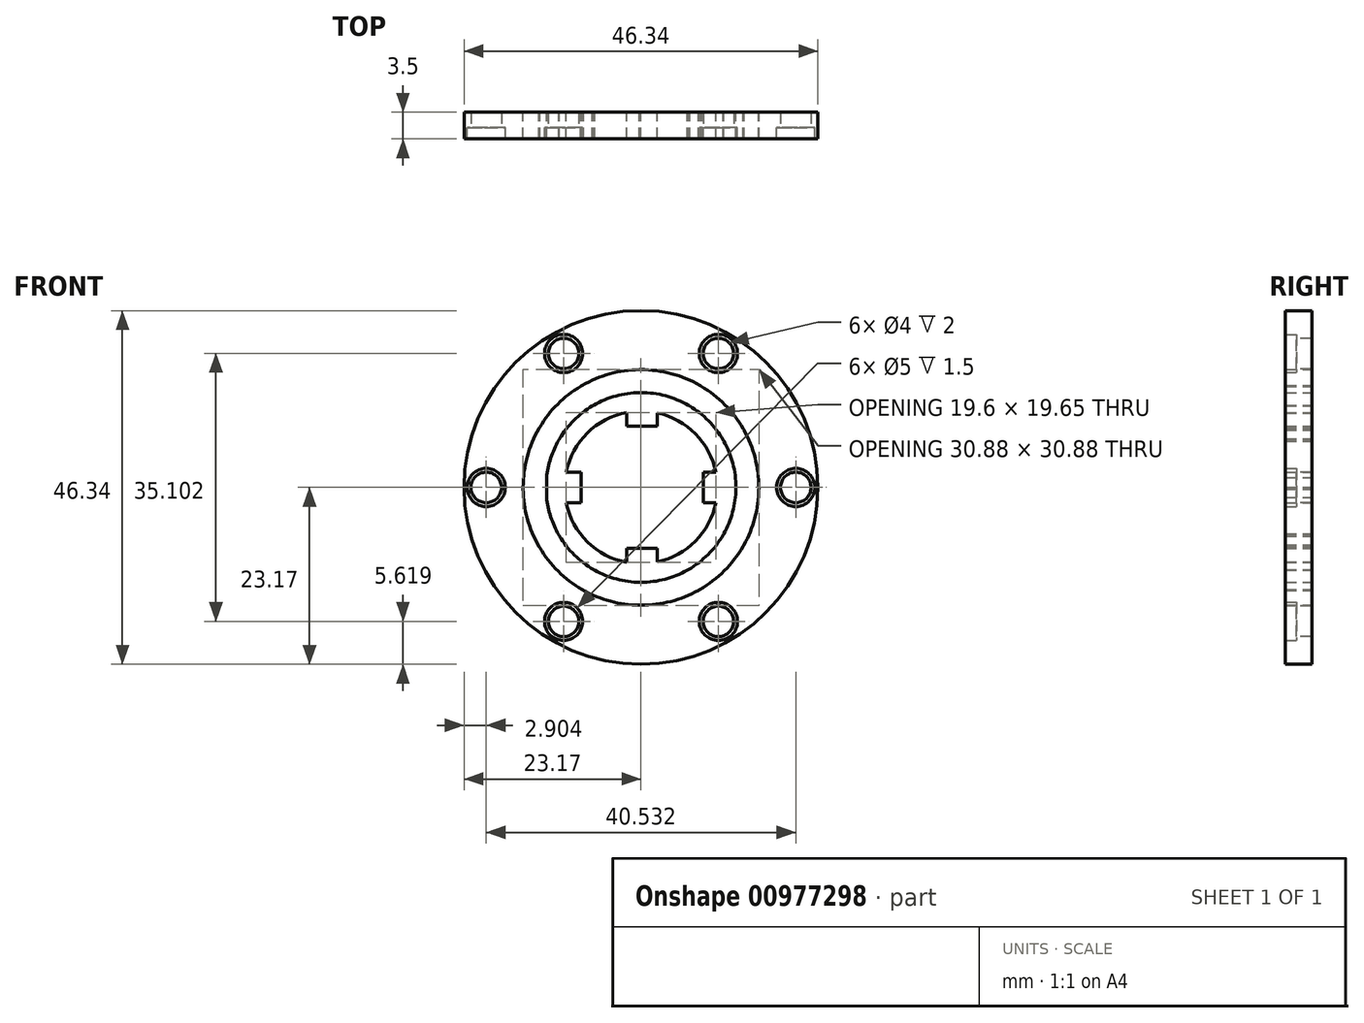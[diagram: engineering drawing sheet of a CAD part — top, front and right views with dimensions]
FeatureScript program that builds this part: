
annotation { "Feature Type Name" : "Feature", "Feature Type Description" : "" }
export const myFeature = defineFeature(function(context is Context, id is Id, definition is map)
    precondition{}
    {
        {
            var Q0;
            Q0=qCreatedBy(makeId("Front.planeOp"),FACE);
            var sketch = newSketch(context, id + "F0", { "sketchPlane" : qUnion([Q0])});
            skCircle(sketch, "E0", {"center": v(0, 0) * mm, "radius": 10 * mm});
            skPoint(sketch, "E1.left.end.orphan", {"position": v(-12.36, 2) * mm});
            skPoint(sketch, "E2.orphan", {"position": v(-12.64, -2) * mm});
            skPoint(sketch, "E1.right.end.orphan", {"position": v(12.64, 2) * mm});
            skPoint(sketch, "E3.trimOffspring.end.orphan", {"position": v(12.36, -2) * mm});
            skPoint(sketch, "E4.top.end.orphan", {"position": v(1.86, -12.5) * mm});
            skPoint(sketch, "E4.top.start.orphan", {"position": v(-1.86, -12.5) * mm});
            skPoint(sketch, "E4.bottom.end.orphan", {"position": v(1.86, 12.5) * mm});
            skPoint(sketch, "E4.bottom.start.orphan", {"position": v(-1.86, 12.5) * mm});
            skLineSegment(sketch, "E5.bottom", {"start": v(12.64, 2) * mm, "end": v(8.14, 2) * mm});
            skLineSegment(sketch, "E5.top", {"start": v(12.64, -2) * mm, "end": v(8.14, -2) * mm});
            skLineSegment(sketch, "E5.left", {"start": v(12.64, 2) * mm, "end": v(12.64, -2) * mm});
            skLineSegment(sketch, "E5.right", {"start": v(8.14, 2) * mm, "end": v(8.14, -2) * mm});
            skLineSegment(sketch, "E6.bottom", {"start": v(-1.86, 12.5) * mm, "end": v(2.14, 12.5) * mm});
            skLineSegment(sketch, "E6.top", {"start": v(-1.86, 8) * mm, "end": v(2.14, 8) * mm});
            skLineSegment(sketch, "E6.left", {"start": v(-1.86, 12.5) * mm, "end": v(-1.86, 8) * mm});
            skLineSegment(sketch, "E6.right", {"start": v(2.14, 12.5) * mm, "end": v(2.14, 8) * mm});
            skLineSegment(sketch, "E7.bottom", {"start": v(-12.36, 2) * mm, "end": v(-7.86, 2) * mm});
            skLineSegment(sketch, "E7.top", {"start": v(-12.36, -2) * mm, "end": v(-7.86, -2) * mm});
            skLineSegment(sketch, "E7.left", {"start": v(-12.36, 2) * mm, "end": v(-12.36, -2) * mm});
            skLineSegment(sketch, "E7.right", {"start": v(-7.86, 2) * mm, "end": v(-7.86, -2) * mm});
            skLineSegment(sketch, "E8.bottom", {"start": v(-1.86, -12.5) * mm, "end": v(2.14, -12.5) * mm});
            skLineSegment(sketch, "E8.top", {"start": v(-1.86, -8) * mm, "end": v(2.14, -8) * mm});
            skLineSegment(sketch, "E8.left", {"start": v(-1.86, -12.5) * mm, "end": v(-1.86, -8) * mm});
            skLineSegment(sketch, "E8.right", {"start": v(2.14, -12.5) * mm, "end": v(2.14, -8) * mm});
            skCircle(sketch, "E9", {"center": v(0, 0) * mm, "radius": 12.43 * mm});
            skCircle(sketch, "E10", {"center": v(0, 0) * mm, "radius": 15.43 * mm});
            skArc(sketch, "E11", {"start": v(0, 15.43) * mm, "mid": v(-1.6, 13.93) * mm, "end": v(0, 12.43) * mm});
            skArc(sketch, "E12", {"start": v(0, 15.27) * mm, "mid": v(-1.44, 13.93) * mm, "end": v(0, 12.6) * mm});
            skLineSegment(sketch, "E13", {"start": v(0, 15.43) * mm, "end": v(0, 15.27) * mm});
            skLineSegment(sketch, "E14", {"start": v(0, 12.6) * mm, "end": v(0, 12.43) * mm});
            skLineSegment(sketch, "E15", {"start": v(0, 15.69) * mm, "end": v(0, 12.13) * mm, "construction": true});
            skArc(sketch, "E16.MirrorCS", {"start": v(0, -15.43) * mm, "mid": v(-1.6, -13.93) * mm, "end": v(0, -12.43) * mm});
            skArc(sketch, "E17.MirrorCS", {"start": v(0, -15.27) * mm, "mid": v(-1.44, -13.93) * mm, "end": v(0, -12.6) * mm});
            skLineSegment(sketch, "E18.MirrorCS", {"start": v(0, -15.69) * mm, "end": v(0, -12.13) * mm, "construction": true});
            skArc(sketch, "E19.MirrorCS", {"start": v(15.43, 0) * mm, "mid": v(13.93, -1.6) * mm, "end": v(12.43, 0) * mm});
            skArc(sketch, "E20.MirrorCS", {"start": v(15.27, 0) * mm, "mid": v(13.93, -1.44) * mm, "end": v(12.6, 0) * mm});
            skLineSegment(sketch, "E21.MirrorCS", {"start": v(15.69, 0) * mm, "end": v(12.13, 0) * mm, "construction": true});
            skArc(sketch, "E22.MirrorCS", {"start": v(-15.27, 0) * mm, "mid": v(-13.93, -1.44) * mm, "end": v(-12.6, 0) * mm});
            skArc(sketch, "E23.MirrorCS", {"start": v(-15.43, 0) * mm, "mid": v(-13.93, -1.6) * mm, "end": v(-12.43, 0) * mm});
            skLineSegment(sketch, "E24.MirrorCS", {"start": v(-15.69, 0) * mm, "end": v(-12.13, 0) * mm, "construction": true});
            skArc(sketch, "E25.MirrorCS", {"start": v(13.37, 7.72) * mm, "mid": v(12.87, 5.58) * mm, "end": v(10.76, 6.21) * mm});
            skArc(sketch, "E26.MirrorCS", {"start": v(13.22, 7.63) * mm, "mid": v(12.78, 5.72) * mm, "end": v(10.9, 6.3) * mm});
            skLineSegment(sketch, "E27.MirrorCS", {"start": v(13.59, 7.84) * mm, "end": v(10.5, 6.07) * mm, "construction": true});
            skLineSegment(sketch, "E28.MirrorCS", {"start": v(-7.84, 13.59) * mm, "end": v(-6.07, 10.5) * mm, "construction": true});
            skArc(sketch, "E29.MirrorCS", {"start": v(-7.63, 13.22) * mm, "mid": v(-8.21, 11.35) * mm, "end": v(-6.3, 10.9) * mm});
            skArc(sketch, "E30.MirrorCS", {"start": v(-7.72, 13.37) * mm, "mid": v(-8.35, 11.26) * mm, "end": v(-6.21, 10.76) * mm});
            skLineSegment(sketch, "E31.MirrorCS", {"start": v(-13.59, -7.84) * mm, "end": v(-10.5, -6.07) * mm, "construction": true});
            skArc(sketch, "E32.MirrorCS", {"start": v(-13.22, -7.63) * mm, "mid": v(-11.35, -8.21) * mm, "end": v(-10.9, -6.3) * mm});
            skArc(sketch, "E33.MirrorCS", {"start": v(-13.37, -7.72) * mm, "mid": v(-11.26, -8.35) * mm, "end": v(-10.76, -6.21) * mm});
            skLineSegment(sketch, "E34.MirrorCS", {"start": v(7.84, -13.59) * mm, "end": v(6.07, -10.5) * mm, "construction": true});
            skArc(sketch, "E35.MirrorCS", {"start": v(7.63, -13.22) * mm, "mid": v(5.72, -12.78) * mm, "end": v(6.3, -10.9) * mm});
            skArc(sketch, "E36.MirrorCS", {"start": v(7.72, -13.37) * mm, "mid": v(5.58, -12.87) * mm, "end": v(6.21, -10.76) * mm});
            skArc(sketch, "E37.MirrorCS", {"start": v(-13.37, 7.72) * mm, "mid": v(-11.26, 8.35) * mm, "end": v(-10.76, 6.21) * mm});
            skArc(sketch, "E38.MirrorCS", {"start": v(-13.22, 7.63) * mm, "mid": v(-11.35, 8.21) * mm, "end": v(-10.9, 6.3) * mm});
            skLineSegment(sketch, "E39.MirrorCS", {"start": v(-13.59, 7.84) * mm, "end": v(-10.5, 6.07) * mm, "construction": true});
            skArc(sketch, "E40.MirrorCS", {"start": v(7.63, 13.22) * mm, "mid": v(8.21, 11.35) * mm, "end": v(6.3, 10.9) * mm});
            skLineSegment(sketch, "E41.MirrorCS", {"start": v(7.84, 13.59) * mm, "end": v(6.07, 10.5) * mm, "construction": true});
            skArc(sketch, "E42.MirrorCS", {"start": v(7.72, 13.37) * mm, "mid": v(8.35, 11.26) * mm, "end": v(6.21, 10.76) * mm});
            skArc(sketch, "E43.MirrorCS", {"start": v(13.37, -7.72) * mm, "mid": v(12.87, -5.58) * mm, "end": v(10.76, -6.21) * mm});
            skArc(sketch, "E44.MirrorCS", {"start": v(13.22, -7.63) * mm, "mid": v(12.78, -5.72) * mm, "end": v(10.9, -6.3) * mm});
            skLineSegment(sketch, "E45.MirrorCS", {"start": v(13.59, -7.84) * mm, "end": v(10.5, -6.07) * mm, "construction": true});
            skArc(sketch, "E46.MirrorCS", {"start": v(-7.72, -13.37) * mm, "mid": v(-5.58, -12.87) * mm, "end": v(-6.21, -10.76) * mm});
            skArc(sketch, "E47.MirrorCS", {"start": v(-7.63, -13.22) * mm, "mid": v(-5.72, -12.78) * mm, "end": v(-6.3, -10.9) * mm});
            skLineSegment(sketch, "E48.MirrorCS", {"start": v(-7.84, -13.59) * mm, "end": v(-6.07, -10.5) * mm, "construction": true});
            skCircle(sketch, "E49", {"center": v(0, 0) * mm, "radius": 20.27 * mm, "construction": true});
            skCircle(sketch, "E50", {"center": v(0, 0) * mm, "radius": 23.17 * mm});
            skLineSegment(sketch, "E51.0", {"start": v(20.27, 0) * mm, "end": v(10.13, -17.55) * mm});
            skLineSegment(sketch, "E51.1", {"start": v(10.13, -17.55) * mm, "end": v(-10.13, -17.55) * mm});
            skLineSegment(sketch, "E51.2", {"start": v(-10.13, -17.55) * mm, "end": v(-20.27, 0) * mm});
            skLineSegment(sketch, "E51.3", {"start": v(-20.27, 0) * mm, "end": v(-10.13, 17.55) * mm});
            skLineSegment(sketch, "E51.4", {"start": v(-10.13, 17.55) * mm, "end": v(10.13, 17.55) * mm});
            skLineSegment(sketch, "E51.5", {"start": v(10.13, 17.55) * mm, "end": v(20.27, 0) * mm});
            skSolve(sketch);
        }
        {
            var Q0;
            {var subQ3=sQuery(id+"F0.wireOp",EDGE,"E6.left");var subQ5=sQuery(id+"F0.wireOp",EDGE,"E0");var subQ6=makeQuery(id+"F0.imprint","INTERSECT",VERTEX,{"derivedFrom":[subQ5,subQ3]});Q0=makeQuery(id+"F0.imprint","IMPRINT",FACE,{"disambiguationData":[TD([[makeQuery(id+"F0.imprint","IMPRINT",EDGE,{"disambiguationData":[TD([[subQ6,-1.0]])],"derivedFrom":subQ5}),-1.0]])]});}
            var Q1;
            {var subQ5=sQuery(id+"F0.wireOp",EDGE,"E0");var subQ8=sQuery(id+"F0.wireOp",EDGE,"E7.bottom");var subQ9=makeQuery(id+"F0.imprint","INTERSECT",VERTEX,{"derivedFrom":[subQ5,subQ8]});Q1=makeQuery(id+"F0.imprint","IMPRINT",FACE,{"disambiguationData":[TD([[makeQuery(id+"F0.imprint","IMPRINT",EDGE,{"disambiguationData":[TD([[subQ9,-1.0]])],"derivedFrom":subQ5}),-1.0]])]});}
            var Q2;
            {var subQ5=sQuery(id+"F0.wireOp",EDGE,"E7.right");Q2=makeQuery(id+"F0.imprint","IMPRINT",FACE,{"disambiguationData":[TD([[makeQuery(id+"F0.imprint","IMPRINT",EDGE,{"derivedFrom":subQ5}),-1.0]])]});}
            var Q3;
            {var subQ3=sQuery(id+"F0.wireOp",EDGE,"E7.top");var subQ6=sQuery(id+"F0.wireOp",EDGE,"E0");var subQ9=makeQuery(id+"F0.imprint","INTERSECT",VERTEX,{"derivedFrom":[subQ6,subQ3]});Q3=makeQuery(id+"F0.imprint","IMPRINT",FACE,{"disambiguationData":[TD([[makeQuery(id+"F0.imprint","IMPRINT",EDGE,{"disambiguationData":[TD([[subQ9,-1.0]])],"derivedFrom":subQ6}),-1.0]])]});}
            var Q4;
            {var subQ1=sQuery(id+"F0.wireOp",EDGE,"E8.left");var subQ5=sQuery(id+"F0.wireOp",EDGE,"E0");var subQ6=makeQuery(id+"F0.imprint","INTERSECT",VERTEX,{"derivedFrom":[subQ5,subQ1]});Q4=makeQuery(id+"F0.imprint","IMPRINT",FACE,{"disambiguationData":[TD([[makeQuery(id+"F0.imprint","IMPRINT",EDGE,{"disambiguationData":[TD([[subQ6,-1.0]])],"derivedFrom":subQ5}),-1.0]])]});}
            var Q5;
            {var subQ5=sQuery(id+"F0.wireOp",EDGE,"E8.top");Q5=makeQuery(id+"F0.imprint","IMPRINT",FACE,{"disambiguationData":[TD([[makeQuery(id+"F0.imprint","IMPRINT",EDGE,{"derivedFrom":subQ5}),-1.0]])]});}
            var Q6;
            {var subQ1=sQuery(id+"F0.wireOp",EDGE,"E8.right");var subQ5=sQuery(id+"F0.wireOp",EDGE,"E0");var subQ6=makeQuery(id+"F0.imprint","INTERSECT",VERTEX,{"derivedFrom":[subQ5,subQ1]});Q6=makeQuery(id+"F0.imprint","IMPRINT",FACE,{"disambiguationData":[TD([[makeQuery(id+"F0.imprint","IMPRINT",EDGE,{"disambiguationData":[TD([[subQ6,-1.0]])],"derivedFrom":subQ5}),-1.0]])]});}
            var Q7;
            {var subQ0=sQuery(id+"F0.wireOp",EDGE,"E5.bottom");var subQ1=sQuery(id+"F0.wireOp",EDGE,"E0");var subQ2=makeQuery(id+"F0.imprint","INTERSECT",VERTEX,{"derivedFrom":[subQ1,subQ0]});Q7=makeQuery(id+"F0.imprint","IMPRINT",FACE,{"disambiguationData":[TD([[makeQuery(id+"F0.imprint","IMPRINT",EDGE,{"disambiguationData":[TD([[subQ2,1.0]])],"derivedFrom":subQ1}),-1.0]])]});}
            var Q8;
            {var subQ5=sQuery(id+"F0.wireOp",EDGE,"E5.right");Q8=makeQuery(id+"F0.imprint","IMPRINT",FACE,{"disambiguationData":[TD([[makeQuery(id+"F0.imprint","IMPRINT",EDGE,{"derivedFrom":subQ5}),1.0]])]});}
            var Q9;
            {var subQ5=sQuery(id+"F0.wireOp",EDGE,"E6.right");var subQ6=sQuery(id+"F0.wireOp",EDGE,"E0");var subQ7=makeQuery(id+"F0.imprint","INTERSECT",VERTEX,{"derivedFrom":[subQ6,subQ5]});Q9=makeQuery(id+"F0.imprint","IMPRINT",FACE,{"disambiguationData":[TD([[makeQuery(id+"F0.imprint","IMPRINT",EDGE,{"disambiguationData":[TD([[subQ7,1.0]])],"derivedFrom":subQ6}),-1.0]])]});}
            var Q10;
            {var subQ3=sQuery(id+"F0.wireOp",EDGE,"E6.right");var subQ7=sQuery(id+"F0.wireOp",EDGE,"E0");var subQ10=makeQuery(id+"F0.imprint","INTERSECT",VERTEX,{"derivedFrom":[subQ7,subQ3]});Q10=makeQuery(id+"F0.imprint","IMPRINT",FACE,{"disambiguationData":[TD([[makeQuery(id+"F0.imprint","IMPRINT",EDGE,{"disambiguationData":[TD([[subQ10,-1.0]])],"derivedFrom":subQ7}),-1.0]])]});}
            var Q11;
            {var subQ5=sQuery(id+"F0.wireOp",EDGE,"E6.top");Q11=makeQuery(id+"F0.imprint","IMPRINT",FACE,{"disambiguationData":[TD([[makeQuery(id+"F0.imprint","IMPRINT",EDGE,{"derivedFrom":subQ5}),1.0]])]});}
            var Q12;
            Q12=makeQuery(id+"F0.imprint","IMPRINT",FACE,{"disambiguationData":[TD([[makeQuery(id+"F0.imprint","IMPRINT",EDGE,{"derivedFrom":sQuery(id+"F0.wireOp",EDGE,"E50")}),1.0]])]});
            var Q13;
            Q13=makeQuery(id+"F0.imprint","IMPRINT",FACE,{"disambiguationData":[TD([[makeQuery(id+"F0.imprint","IMPRINT",EDGE,{"derivedFrom":sQuery(id+"F0.wireOp",EDGE,"E51.0")}),-1.0]])]});
            extrude(context, id + "F1", {"entities" : qUnion([Q0, Q1, Q2, Q3, Q4, Q5, Q6, Q7, Q8, Q9, Q10, Q11, Q12, Q13]), "depth" : 1.5 * mm, "offsetDistance" : 25 * mm, "hasSecondDirection" : true, "secondDirectionOppositeDirection" : true, "secondDirectionDepth" : 2 * mm});
        }
        {
            var Q0;
            Q0=sQuery(id+"F0.wireOp",EDGE,"E11");
            var Q1;
            Q1=sQuery(id+"F0.wireOp",EDGE,"E12");
            var Q2;
            Q2=sQuery(id+"F0.wireOp",EDGE,"E15");
            revolve(context, id + "F2", {"bodyType" : ToolBodyType.SURFACE, "surfaceOperationType" : NewSurfaceOperationType.NEW, "surfaceEntities" : qUnion([Q0, Q1]), "axis" : qUnion([Q2]), "revolveType" : RevolveType.FULL});
        }
        {
            var Q0;
            Q0=sQuery(id+"F0.wireOp",EDGE,"E40.MirrorCS");
            var Q1;
            Q1=sQuery(id+"F0.wireOp",EDGE,"E42.MirrorCS");
            var Q2;
            Q2=sQuery(id+"F0.wireOp",EDGE,"E41.MirrorCS");
            revolve(context, id + "F3", {"bodyType" : ToolBodyType.SURFACE, "surfaceOperationType" : NewSurfaceOperationType.NEW, "surfaceEntities" : qUnion([Q0, Q1]), "axis" : qUnion([Q2]), "revolveType" : RevolveType.FULL});
        }
        {
            var Q0;
            Q0=sQuery(id+"F0.wireOp",EDGE,"E25.MirrorCS");
            var Q1;
            Q1=sQuery(id+"F0.wireOp",EDGE,"E26.MirrorCS");
            var Q2;
            Q2=sQuery(id+"F0.wireOp",EDGE,"E27.MirrorCS");
            revolve(context, id + "F4", {"bodyType" : ToolBodyType.SURFACE, "surfaceOperationType" : NewSurfaceOperationType.NEW, "surfaceEntities" : qUnion([Q0, Q1]), "axis" : qUnion([Q2]), "revolveType" : RevolveType.FULL});
        }
        {
            var Q0;
            Q0=sQuery(id+"F0.wireOp",EDGE,"E20.MirrorCS");
            var Q1;
            Q1=sQuery(id+"F0.wireOp",EDGE,"E19.MirrorCS");
            var Q2;
            Q2=sQuery(id+"F0.wireOp",EDGE,"E21.MirrorCS");
            revolve(context, id + "F5", {"bodyType" : ToolBodyType.SURFACE, "surfaceOperationType" : NewSurfaceOperationType.NEW, "surfaceEntities" : qUnion([Q0, Q1]), "axis" : qUnion([Q2]), "revolveType" : RevolveType.FULL});
        }
        {
            var Q0;
            Q0=sQuery(id+"F0.wireOp",EDGE,"E22.MirrorCS");
            var Q1;
            Q1=sQuery(id+"F0.wireOp",EDGE,"E23.MirrorCS");
            var Q2;
            Q2=sQuery(id+"F0.wireOp",EDGE,"E24.MirrorCS");
            revolve(context, id + "F6", {"bodyType" : ToolBodyType.SURFACE, "surfaceOperationType" : NewSurfaceOperationType.NEW, "surfaceEntities" : qUnion([Q0, Q1]), "axis" : qUnion([Q2]), "revolveType" : RevolveType.FULL});
        }
        {
            var Q0;
            Q0=sQuery(id+"F0.wireOp",EDGE,"E29.MirrorCS");
            var Q1;
            Q1=sQuery(id+"F0.wireOp",EDGE,"E30.MirrorCS");
            var Q2;
            Q2=sQuery(id+"F0.wireOp",EDGE,"E28.MirrorCS");
            revolve(context, id + "F7", {"bodyType" : ToolBodyType.SURFACE, "surfaceOperationType" : NewSurfaceOperationType.NEW, "surfaceEntities" : qUnion([Q0, Q1]), "axis" : qUnion([Q2]), "revolveType" : RevolveType.FULL});
        }
        {
            var Q0;
            Q0=sQuery(id+"F0.wireOp",EDGE,"E37.MirrorCS");
            var Q1;
            Q1=sQuery(id+"F0.wireOp",EDGE,"E38.MirrorCS");
            var Q2;
            Q2=sQuery(id+"F0.wireOp",EDGE,"E39.MirrorCS");
            revolve(context, id + "F8", {"bodyType" : ToolBodyType.SURFACE, "surfaceOperationType" : NewSurfaceOperationType.NEW, "surfaceEntities" : qUnion([Q0, Q1]), "axis" : qUnion([Q2]), "revolveType" : RevolveType.FULL});
        }
        {
            var Q0;
            Q0=sQuery(id+"F0.wireOp",EDGE,"E33.MirrorCS");
            var Q1;
            Q1=sQuery(id+"F0.wireOp",EDGE,"E32.MirrorCS");
            var Q2;
            Q2=sQuery(id+"F0.wireOp",EDGE,"E31.MirrorCS");
            revolve(context, id + "F9", {"bodyType" : ToolBodyType.SURFACE, "surfaceOperationType" : NewSurfaceOperationType.NEW, "surfaceEntities" : qUnion([Q0, Q1]), "axis" : qUnion([Q2]), "revolveType" : RevolveType.FULL});
        }
        {
            var Q0;
            Q0=sQuery(id+"F0.wireOp",EDGE,"E46.MirrorCS");
            var Q1;
            Q1=sQuery(id+"F0.wireOp",EDGE,"E47.MirrorCS");
            var Q2;
            Q2=sQuery(id+"F0.wireOp",EDGE,"E48.MirrorCS");
            revolve(context, id + "F10", {"bodyType" : ToolBodyType.SURFACE, "surfaceOperationType" : NewSurfaceOperationType.NEW, "surfaceEntities" : qUnion([Q0, Q1]), "axis" : qUnion([Q2]), "revolveType" : RevolveType.FULL});
        }
        {
            var Q0;
            Q0=sQuery(id+"F0.wireOp",EDGE,"E16.MirrorCS");
            var Q1;
            Q1=sQuery(id+"F0.wireOp",EDGE,"E17.MirrorCS");
            var Q2;
            Q2=sQuery(id+"F0.wireOp",EDGE,"E18.MirrorCS");
            revolve(context, id + "F11", {"bodyType" : ToolBodyType.SURFACE, "surfaceOperationType" : NewSurfaceOperationType.NEW, "surfaceEntities" : qUnion([Q0, Q1]), "axis" : qUnion([Q2]), "revolveType" : RevolveType.FULL});
        }
        {
            var Q0;
            Q0=sQuery(id+"F0.wireOp",EDGE,"E35.MirrorCS");
            var Q1;
            Q1=sQuery(id+"F0.wireOp",EDGE,"E36.MirrorCS");
            var Q2;
            Q2=sQuery(id+"F0.wireOp",EDGE,"E34.MirrorCS");
            revolve(context, id + "F12", {"bodyType" : ToolBodyType.SURFACE, "surfaceOperationType" : NewSurfaceOperationType.NEW, "surfaceEntities" : qUnion([Q0, Q1]), "axis" : qUnion([Q2]), "revolveType" : RevolveType.FULL});
        }
        {
            var Q0;
            Q0=sQuery(id+"F0.wireOp",EDGE,"E43.MirrorCS");
            var Q1;
            Q1=sQuery(id+"F0.wireOp",EDGE,"E44.MirrorCS");
            var Q2;
            Q2=sQuery(id+"F0.wireOp",EDGE,"E45.MirrorCS");
            revolve(context, id + "F13", {"bodyType" : ToolBodyType.SURFACE, "surfaceOperationType" : NewSurfaceOperationType.NEW, "surfaceEntities" : qUnion([Q0, Q1]), "axis" : qUnion([Q2]), "revolveType" : RevolveType.FULL});
        }
        {
            var Q0;
            Q0=sQuery(id+"F0.wireOp",VERTEX,"E51.2.end");
            var Q1;
            Q1=sQuery(id+"F0.wireOp",VERTEX,"E51.1.end");
            var Q2;
            Q2=sQuery(id+"F0.wireOp",VERTEX,"E51.0.end");
            var Q3;
            Q3=sQuery(id+"F0.wireOp",VERTEX,"E51.0.start");
            var Q4;
            Q4=sQuery(id+"F0.wireOp",VERTEX,"E51.4.end");
            var Q5;
            Q5=sQuery(id+"F0.wireOp",VERTEX,"E51.3.end");
            var Q6;
            Q6=makeQuery(id+"F1.opExtrude","SWEPT_BODY",BODY,{"disambiguationData":[OSD([sQuery(id+"F0.wireOp",EDGE,"E10"),sQuery(id+"F0.wireOp",EDGE,"E11"),sQuery(id+"F0.wireOp",EDGE,"E16.MirrorCS"),sQuery(id+"F0.wireOp",EDGE,"E19.MirrorCS"),sQuery(id+"F0.wireOp",EDGE,"E23.MirrorCS"),sQuery(id+"F0.wireOp",EDGE,"E30.MirrorCS"),sQuery(id+"F0.wireOp",EDGE,"E33.MirrorCS"),sQuery(id+"F0.wireOp",EDGE,"E36.MirrorCS"),sQuery(id+"F0.wireOp",EDGE,"E37.MirrorCS"),sQuery(id+"F0.wireOp",EDGE,"E42.MirrorCS"),sQuery(id+"F0.wireOp",EDGE,"E25.MirrorCS"),sQuery(id+"F0.wireOp",EDGE,"E43.MirrorCS"),sQuery(id+"F0.wireOp",EDGE,"E46.MirrorCS"),sQuery(id+"F0.wireOp",EDGE,"E50")])]});
            hole(context, id + "F14", {"style" : HoleStyle.SIMPLE, "endStyle" : HoleEndStyle.THROUGH, "holeDiameter" : 4 * mm, "majorDiameter" : 5 * mm, "isTappedThrough" : true, "tappedDepth" : 12 * mm, "tapClearance" : 3, "locations" : qUnion([Q0, Q1, Q2, Q3, Q4, Q5]), "scope" : qUnion([Q6])});
        }
        {
            var Q0;
            Q0=sQuery(id+"F0.wireOp",VERTEX,"E51.0.end");
            var Q1;
            Q1=sQuery(id+"F0.wireOp",VERTEX,"E51.1.end");
            var Q2;
            Q2=sQuery(id+"F0.wireOp",VERTEX,"E51.2.end");
            var Q3;
            Q3=sQuery(id+"F0.wireOp",VERTEX,"E51.3.end");
            var Q4;
            Q4=sQuery(id+"F0.wireOp",VERTEX,"E51.4.end");
            var Q5;
            Q5=sQuery(id+"F0.wireOp",VERTEX,"E51.0.start");
            var Q6;
            Q6=makeQuery(id+"F1.opExtrude","SWEPT_BODY",BODY,{"disambiguationData":[OSD([sQuery(id+"F0.wireOp",EDGE,"E10"),sQuery(id+"F0.wireOp",EDGE,"E11"),sQuery(id+"F0.wireOp",EDGE,"E16.MirrorCS"),sQuery(id+"F0.wireOp",EDGE,"E19.MirrorCS"),sQuery(id+"F0.wireOp",EDGE,"E23.MirrorCS"),sQuery(id+"F0.wireOp",EDGE,"E30.MirrorCS"),sQuery(id+"F0.wireOp",EDGE,"E33.MirrorCS"),sQuery(id+"F0.wireOp",EDGE,"E36.MirrorCS"),sQuery(id+"F0.wireOp",EDGE,"E37.MirrorCS"),sQuery(id+"F0.wireOp",EDGE,"E42.MirrorCS"),sQuery(id+"F0.wireOp",EDGE,"E25.MirrorCS"),sQuery(id+"F0.wireOp",EDGE,"E43.MirrorCS"),sQuery(id+"F0.wireOp",EDGE,"E46.MirrorCS"),sQuery(id+"F0.wireOp",EDGE,"E50")])]});
            hole(context, id + "F15", {"style" : HoleStyle.SIMPLE, "endStyle" : HoleEndStyle.BLIND, "oppositeDirection" : true, "holeDiameter" : 5 * mm, "majorDiameter" : 5 * mm, "holeDepth" : 2 * mm, "isTappedThrough" : true, "tappedDepth" : 12 * mm, "tapClearance" : 3, "locations" : qUnion([Q0, Q1, Q2, Q3, Q4, Q5]), "scope" : qUnion([Q6])});
        }
    });
